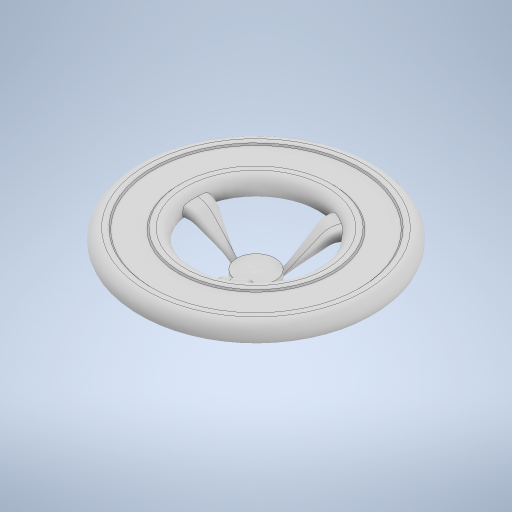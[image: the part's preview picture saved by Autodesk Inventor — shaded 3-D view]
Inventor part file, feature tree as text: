
AUTODESK INVENTOR PART (.ipt)
format: ipt  version: 2023 (Build 270158000, 158)  size: 540,160 bytes
history: native  units: mm
features: sketch x4, other x2, revolve x1, loft x1, pattern_circular x1
ambient origin geometry x8: Origin, YZ Plane, XZ Plane, XY Plane, X Axis, Y Axis, Z Axis, Center Point
bodies: Solido1 (feature_tree)
feature tree (9):
  revolve  "Rivoluzione1"
  sketch  "Schizzo2"
  sketch  "Schizzo3"
  sketch  "Schizzo 3D2"
  loft  "Loft1"
  pattern_circular  "Serie circolare1"  [2 undecoded]
  sketch  "Schizzo1"
  other  "Proietta su superficie1"
  other  "Proietta su superficie2"
note: 2 required parameter values undecoded (feature->parameter linkage not recoverable at this tier; creation-order binding heuristic only, values carry confidence <= 0.55)
